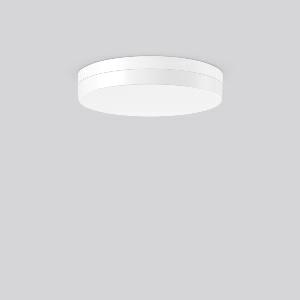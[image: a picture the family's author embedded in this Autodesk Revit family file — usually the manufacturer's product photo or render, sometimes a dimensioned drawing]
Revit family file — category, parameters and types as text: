
# Revit family: flat_slim_round_312676_002_19_d94c
name_source: partatom
category: Lighting Fixtures
units: mm (PartAtom-declared; Revit-internal decimal feet)

## family parameters
Cut with Voids When Loaded = No
Host = Face
Light Source = No
Part Type = Normal
Room Calculation Point = No
Round Connector Dimension = Use Diameter
Shared = No

## types (1)
- MultiLumen 1 830 (1 x LED Modul 830, 2400 lm, 3000)
    Apparent Load = 20 VA
    CIE Flux Codes = 39 70 90 83 100
    Color Rendering = 80
    Color Temperature = 3000
    Default Elevation = 1800 mm
    Height = 70 mm
    Lamp = 1 x LED Modul 830
    Lamp Light Flux = 2400 lm
    Lamp count = 1
    Length = 400 mm
    Lifetime = 50000 h
    Luminous efficacy = 120 lm/W
    Manufacturer = RZB
    ModVariant = No
    Model = 312676.002.19
    Mounting Place = Ceiling
    Mounting Type = Surface mounted
    Number of Poles = 1
    OnlyDefault = Yes
    Power Factor = 1
    Product Name = FLAT SLIM round
    Product group = Surface mounted ceiling and wall luminaires
    ProductGroupID = 305
    Protection Class = Protection class I
    Protection Degree = Degree of protection
    RLX_Detail_Level = 1
    RLX_Emergency_Light_Flux = 0 lm
    RLX_Emergency_Type = 0
    RLX_Emergency_Type_DB = No
    RlxData = <blob elided: 20605 chars, md5=4dc09ead>
    Socket = socket
    Standby Power = 0 W
    System Light Flux = 2400 lm
    System Power = 20 W
    Type Comments = MultiLumen 1 830
    Type Image = 312631.002.jpg
    URL = http://relux.com
    VarID = multilumen_1_830
    Voltage = 0 V
    Weight = 0.00 kg
    Width = 0 mm  [stored 0 ft]

note: [stored X ft] marks values corroborated as IEEE doubles in the binary element streams (Revit-internal decimal feet)

## geometry (parser evidence)
native form markers: Blend x4, Sweep x13
no freeform markers — native parametric forms only
